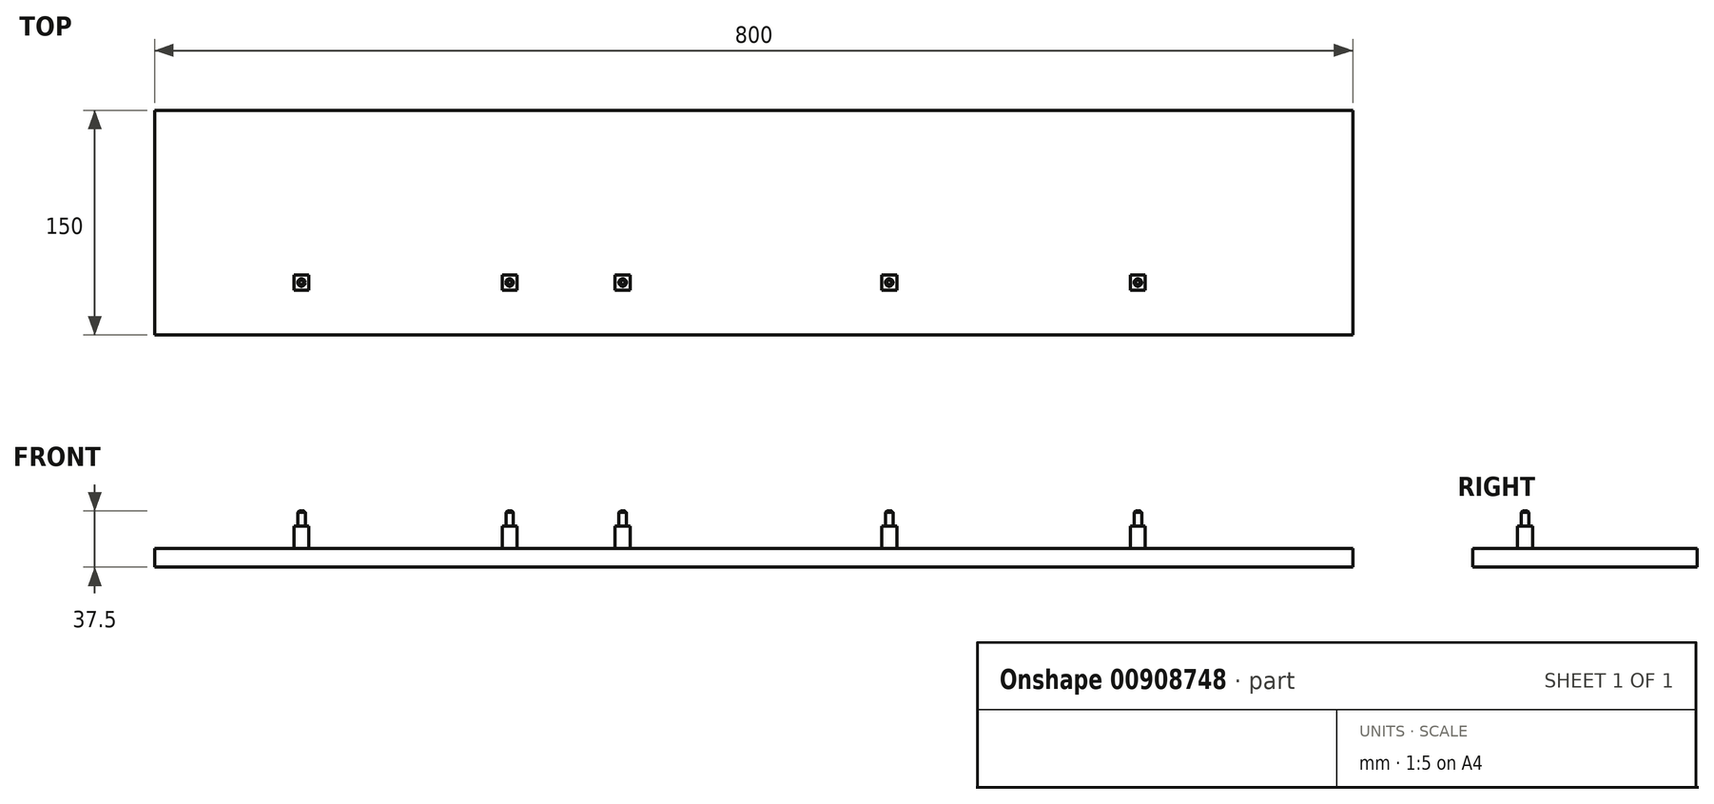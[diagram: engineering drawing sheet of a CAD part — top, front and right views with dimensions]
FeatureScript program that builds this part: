
annotation { "Feature Type Name" : "Feature", "Feature Type Description" : "" }
export const myFeature = defineFeature(function(context is Context, id is Id, definition is map)
    precondition{}
    {
        {
            var Q0;
            Q0=qCreatedBy(makeId("Top.planeOp"),FACE);
            var sketch = newSketch(context, id + "F0", { "sketchPlane" : qUnion([Q0])});
            skLineSegment(sketch, "E0.bottom", {"start": v(400, 75) * mm, "end": v(-400, 75) * mm});
            skLineSegment(sketch, "E0.top", {"start": v(400, -75) * mm, "end": v(-400, -75) * mm});
            skLineSegment(sketch, "E0.left", {"start": v(400, 75) * mm, "end": v(400, -75) * mm});
            skLineSegment(sketch, "E0.right", {"start": v(-400, 75) * mm, "end": v(-400, -75) * mm});
            skPoint(sketch, "E0.middle", {"position": v(0, 0) * mm});
            skSolve(sketch);
        }
        {
            var Q0;
            Q0 = qSketchRegion(id + "F0", true);
            extrude(context, id + "F1", {"entities" : qUnion([Q0]), "depth" : 12.5 * mm, "offsetDistance" : 25 * mm});
        }
        {
            var Q0;
            Q0=makeQuery(id+"F1.opExtrude","CAP_FACE",FACE,{"disambiguationData":[OSD([sQuery(id+"F0.wireOp",EDGE,"E0.bottom"),sQuery(id+"F0.wireOp",EDGE,"E0.top"),sQuery(id+"F0.wireOp",EDGE,"E0.left"),sQuery(id+"F0.wireOp",EDGE,"E0.right")])],"isStart":false});
            var sketch = newSketch(context, id + "F2", { "sketchPlane" : qUnion([Q0])});
            skLineSegment(sketch, "E1", {"start": v(-400, -75) * mm, "end": v(-302, -75) * mm, "construction": true});
            skLineSegment(sketch, "E2", {"start": v(-302, -75) * mm, "end": v(-302, -40) * mm, "construction": true});
            skLineSegment(sketch, "E3.bottom", {"start": v(-297, -45) * mm, "end": v(-307, -45) * mm});
            skLineSegment(sketch, "E3.top", {"start": v(-297, -35) * mm, "end": v(-307, -35) * mm});
            skLineSegment(sketch, "E3.left", {"start": v(-297, -45) * mm, "end": v(-297, -35) * mm});
            skLineSegment(sketch, "E3.right", {"start": v(-307, -45) * mm, "end": v(-307, -35) * mm});
            skPoint(sketch, "E3.middle", {"position": v(-302, -40) * mm});
            skLineSegment(sketch, "E4", {"start": v(-302, -40) * mm, "end": v(-163, -40) * mm, "construction": true});
            skLineSegment(sketch, "E5.bottom", {"start": v(-158, -45) * mm, "end": v(-168, -45) * mm});
            skLineSegment(sketch, "E5.top", {"start": v(-158, -35) * mm, "end": v(-168, -35) * mm});
            skLineSegment(sketch, "E5.left", {"start": v(-158, -45) * mm, "end": v(-158, -35) * mm});
            skLineSegment(sketch, "E5.right", {"start": v(-168, -45) * mm, "end": v(-168, -35) * mm});
            skPoint(sketch, "E5.middle", {"position": v(-163, -40) * mm});
            skLineSegment(sketch, "E6", {"start": v(-163, -40) * mm, "end": v(-87.5, -40) * mm, "construction": true});
            skPoint(sketch, "E6.endSnap0", {"position": v(-158, -40) * mm});
            skLineSegment(sketch, "E7.bottom", {"start": v(-82.5, -45) * mm, "end": v(-92.5, -45) * mm});
            skLineSegment(sketch, "E7.top", {"start": v(-82.5, -35) * mm, "end": v(-92.5, -35) * mm});
            skLineSegment(sketch, "E7.left", {"start": v(-82.5, -45) * mm, "end": v(-82.5, -35) * mm});
            skLineSegment(sketch, "E7.right", {"start": v(-92.5, -45) * mm, "end": v(-92.5, -35) * mm});
            skPoint(sketch, "E7.middle", {"position": v(-87.5, -40) * mm});
            skLineSegment(sketch, "E8", {"start": v(-87.5, -40) * mm, "end": v(90.5, -40) * mm, "construction": true});
            skLineSegment(sketch, "E9.bottom", {"start": v(95.5, -45) * mm, "end": v(85.5, -45) * mm});
            skLineSegment(sketch, "E9.top", {"start": v(95.5, -35) * mm, "end": v(85.5, -35) * mm});
            skLineSegment(sketch, "E9.left", {"start": v(95.5, -45) * mm, "end": v(95.5, -35) * mm});
            skLineSegment(sketch, "E9.right", {"start": v(85.5, -45) * mm, "end": v(85.5, -35) * mm});
            skPoint(sketch, "E9.middle", {"position": v(90.5, -40) * mm});
            skLineSegment(sketch, "E10", {"start": v(90.5, -40) * mm, "end": v(256.5, -40) * mm, "construction": true});
            skLineSegment(sketch, "E11.bottom", {"start": v(261.5, -45) * mm, "end": v(251.5, -45) * mm});
            skLineSegment(sketch, "E11.top", {"start": v(261.5, -35) * mm, "end": v(251.5, -35) * mm});
            skLineSegment(sketch, "E11.left", {"start": v(261.5, -45) * mm, "end": v(261.5, -35) * mm});
            skLineSegment(sketch, "E11.right", {"start": v(251.5, -45) * mm, "end": v(251.5, -35) * mm});
            skPoint(sketch, "E11.middle", {"position": v(256.5, -40) * mm});
            skSolve(sketch);
        }
        {
            var Q0;
            Q0 = qSketchRegion(id + "F2", true);
            extrude(context, id + "F3", {"entities" : qUnion([Q0]), "operationType" : NewBodyOperationType.ADD, "depth" : 15 * mm, "offsetDistance" : 25 * mm});
        }
        {
            var Q0;
            Q0=makeQuery(id+"F3.opExtrude","CAP_FACE",FACE,{"disambiguationData":[OSD([sQuery(id+"F2.wireOp",EDGE,"E3.bottom"),sQuery(id+"F2.wireOp",EDGE,"E3.top"),sQuery(id+"F2.wireOp",EDGE,"E3.left"),sQuery(id+"F2.wireOp",EDGE,"E3.right")])],"isStart":false});
            var sketch = newSketch(context, id + "F4", { "sketchPlane" : qUnion([Q0])});
            skCircle(sketch, "E12", {"center": v(-302, -40) * mm, "radius": 2.5 * mm});
            skPoint(sketch, "E12.centerSnap0", {"position": v(-302, -35) * mm});
            skPoint(sketch, "E12.centerSnap1", {"position": v(-297, -40) * mm});
            skSolve(sketch);
        }
        {
            var Q0;
            Q0 = qSketchRegion(id + "F4", true);
            extrude(context, id + "F5", {"entities" : qUnion([Q0]), "operationType" : NewBodyOperationType.ADD, "depth" : 10 * mm, "offsetDistance" : 25 * mm});
        }
        {
            var Q0;
            Q0=makeQuery(id+"F5.opExtrude","CAP_EDGE",EDGE,{"disambiguationData":[OSD([sQuery(id+"F4.wireOp",EDGE,"E12")])],"isStart":false});
            chamfer(context, id + "F6", {"entities" : qUnion([Q0]), "width" : 1 * mm, "tangentPropagation" : true});
        }
        {
            var Q0;
            Q0=makeQuery(id+"F3.opExtrude","CAP_FACE",FACE,{"disambiguationData":[OSD([sQuery(id+"F2.wireOp",EDGE,"E5.bottom"),sQuery(id+"F2.wireOp",EDGE,"E5.top"),sQuery(id+"F2.wireOp",EDGE,"E5.left"),sQuery(id+"F2.wireOp",EDGE,"E5.right")])],"isStart":false});
            var sketch = newSketch(context, id + "F7", { "sketchPlane" : qUnion([Q0])});
            skCircle(sketch, "E13", {"center": v(-163, -40) * mm, "radius": 2.5 * mm});
            skPoint(sketch, "E13.centerSnap0", {"position": v(-158, -40) * mm});
            skPoint(sketch, "E13.centerSnap1", {"position": v(-163, -35) * mm});
            skSolve(sketch);
        }
        {
            var Q0;
            Q0 = qSketchRegion(id + "F7", true);
            extrude(context, id + "F8", {"entities" : qUnion([Q0]), "operationType" : NewBodyOperationType.ADD, "depth" : 10 * mm, "offsetDistance" : 25 * mm});
        }
        {
            var Q0;
            Q0=makeQuery(id+"F3.opExtrude","CAP_FACE",FACE,{"disambiguationData":[OSD([sQuery(id+"F2.wireOp",EDGE,"E7.bottom"),sQuery(id+"F2.wireOp",EDGE,"E7.top"),sQuery(id+"F2.wireOp",EDGE,"E7.left"),sQuery(id+"F2.wireOp",EDGE,"E7.right")])],"isStart":false});
            var sketch = newSketch(context, id + "F9", { "sketchPlane" : qUnion([Q0])});
            skCircle(sketch, "E14", {"center": v(-87.5, -40) * mm, "radius": 2.5 * mm});
            skPoint(sketch, "E14.centerSnap0", {"position": v(-82.5, -40) * mm});
            skPoint(sketch, "E14.centerSnap1", {"position": v(-87.5, -35) * mm});
            skSolve(sketch);
        }
        {
            var Q0;
            Q0 = qSketchRegion(id + "F9", true);
            extrude(context, id + "F10", {"entities" : qUnion([Q0]), "operationType" : NewBodyOperationType.ADD, "depth" : 10 * mm, "offsetDistance" : 25 * mm});
        }
        {
            var Q0;
            Q0=makeQuery(id+"F3.opExtrude","CAP_FACE",FACE,{"disambiguationData":[OSD([sQuery(id+"F2.wireOp",EDGE,"E9.bottom"),sQuery(id+"F2.wireOp",EDGE,"E9.top"),sQuery(id+"F2.wireOp",EDGE,"E9.left"),sQuery(id+"F2.wireOp",EDGE,"E9.right")])],"isStart":false});
            var sketch = newSketch(context, id + "F11", { "sketchPlane" : qUnion([Q0])});
            skCircle(sketch, "E15", {"center": v(90.5, -40) * mm, "radius": 2.5 * mm});
            skPoint(sketch, "E15.centerSnap0", {"position": v(95.5, -40) * mm});
            skPoint(sketch, "E15.centerSnap1", {"position": v(90.5, -35) * mm});
            skSolve(sketch);
        }
        {
            var Q0;
            Q0 = qSketchRegion(id + "F11", true);
            extrude(context, id + "F12", {"entities" : qUnion([Q0]), "operationType" : NewBodyOperationType.ADD, "depth" : 10 * mm, "offsetDistance" : 25 * mm});
        }
        {
            var Q0;
            Q0=makeQuery(id+"F3.opExtrude","CAP_FACE",FACE,{"disambiguationData":[OSD([sQuery(id+"F2.wireOp",EDGE,"E11.bottom"),sQuery(id+"F2.wireOp",EDGE,"E11.top"),sQuery(id+"F2.wireOp",EDGE,"E11.left"),sQuery(id+"F2.wireOp",EDGE,"E11.right")])],"isStart":false});
            var sketch = newSketch(context, id + "F13", { "sketchPlane" : qUnion([Q0])});
            skCircle(sketch, "E16", {"center": v(256.5, -40) * mm, "radius": 2.5 * mm});
            skPoint(sketch, "E16.centerSnap0", {"position": v(261.5, -40) * mm});
            skPoint(sketch, "E16.centerSnap1", {"position": v(256.5, -35) * mm});
            skSolve(sketch);
        }
        {
            var Q0;
            Q0 = qSketchRegion(id + "F13", true);
            extrude(context, id + "F14", {"entities" : qUnion([Q0]), "operationType" : NewBodyOperationType.ADD, "depth" : 10 * mm, "offsetDistance" : 25 * mm});
        }
        {
            var Q0;
            Q0=makeQuery(id+"F14.opExtrude","CAP_EDGE",EDGE,{"disambiguationData":[OSD([sQuery(id+"F13.wireOp",EDGE,"E16")])],"isStart":false});
            var Q1;
            Q1=makeQuery(id+"F12.opExtrude","CAP_EDGE",EDGE,{"disambiguationData":[OSD([sQuery(id+"F11.wireOp",EDGE,"E15")])],"isStart":false});
            var Q2;
            Q2=makeQuery(id+"F10.opExtrude","CAP_EDGE",EDGE,{"disambiguationData":[OSD([sQuery(id+"F9.wireOp",EDGE,"E14")])],"isStart":false});
            var Q3;
            Q3=makeQuery(id+"F8.opExtrude","CAP_EDGE",EDGE,{"disambiguationData":[OSD([sQuery(id+"F7.wireOp",EDGE,"E13")])],"isStart":false});
            chamfer(context, id + "F15", {"entities" : qUnion([Q0, Q1, Q2, Q3]), "width" : 1 * mm, "tangentPropagation" : true});
        }
    });
